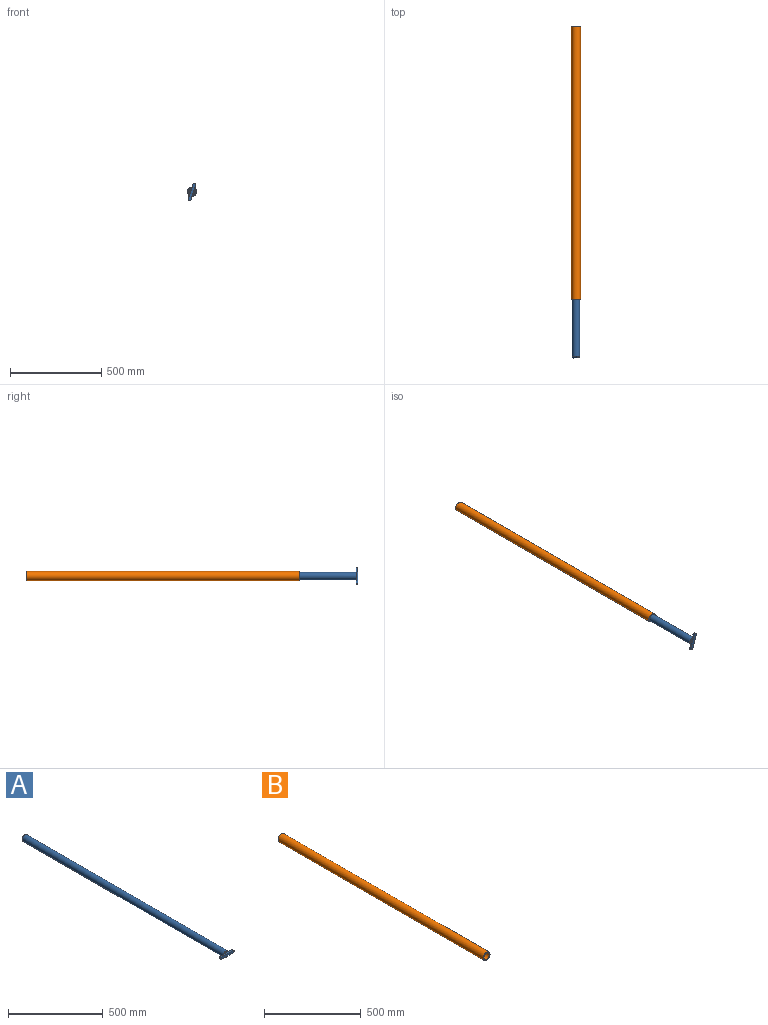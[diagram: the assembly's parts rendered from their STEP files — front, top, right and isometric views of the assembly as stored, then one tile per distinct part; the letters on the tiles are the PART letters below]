
ASSEMBLY  parts=2 mates=1
PART A: 17 faces, bbox 98.2x1510x40 mm
  f0: plane 36.91x12.3mm, normal (0,-1,0), area 195mm2, adj f1,f2,f7
  f1: cylinder r=15mm len=1500mm, axis (0,1,0), area 141371.7mm2, adj f0,f3,f4,f12
  f2: cylinder r=20mm len=1500mm, axis (0,1,0), area 188495.6mm2, adj f0,f3,f4,f5,f6
  f3: plane 36.91x12.3mm, normal (0,-1,0), area 195mm2, adj f1,f2,f9
  f4: plane 40x40mm, normal (0,1,0), area 549.8mm2, adj f1,f2
  f5: plane 30.64x15.41mm, normal (0,1,0), area 445.5mm2, adj f2,f7,f8,f9,f13,f14
  f6: plane 30.64x15.41mm, normal (0,1,0), area 445.5mm2, adj f2,f7,f9,f10,f15,f16
  f7: plane 88.2x10mm, normal (0,0,-1), area 882mm2, adj f0,f5,f6,f11,f12,f13,f16
  f8: plane 10x5.41mm, normal (1,0,0), area 54.1mm2, adj f5,f11,f13,f14
  f9: plane 88.2x10mm, normal (0,0,1), area 882mm2, adj f3,f5,f6,f11,f12,f14,f15
  f10: plane 10x5.41mm, normal (-1,0,0), area 54.1mm2, adj f6,f11,f15,f16
  f11: plane 98.2x15.41mm, normal (0,-1,0), area 1491.8mm2, adj f7,f8,f9,f10,f13,f14,f15,f16
  f12: plane 30x15.41mm, normal (0,1,0), area 441.1mm2, adj f1,f7,f9
  f13: cylinder r=5mm len=10mm, axis (0,-1,0), area 78.5mm2, adj f5,f7,f8,f11
  f14: cylinder r=5mm len=10mm, axis (0,1,0), area 78.5mm2, adj f5,f8,f9,f11
  f15: cylinder r=5mm len=10mm, axis (0,-1,0), area 78.5mm2, adj f6,f9,f10,f11
  f16: cylinder r=5mm len=10mm, axis (0,1,0), area 78.5mm2, adj f6,f7,f10,f11
PART B: 4 faces, bbox 50x1500x50 mm
  f0: cylinder r=20mm len=1500mm, axis (0,1,0), area 188495.6mm2, adj f2,f3
  f1: cylinder r=25mm len=1500mm, axis (0,1,0), area 235619.4mm2, adj f2,f3
  f2: plane 50x50mm, normal (0,-1,0), area 706.9mm2, adj f0,f1
  f3: plane 50x50mm, normal (0,1,0), area 706.9mm2, adj f0,f1
PLACE A rot(axis=(0,1,0),108.4deg) t=(91.62,369.92,-1454.88)mm
PLACE B rot(axis=(0,-1,0),173.2deg) t=(91.62,681.61,-1454.88)mm fixed
MATE cylindrical B.f0 <-> A.f2  axis (0,1,0) through (91.62,681.61,-1454.88)mm
